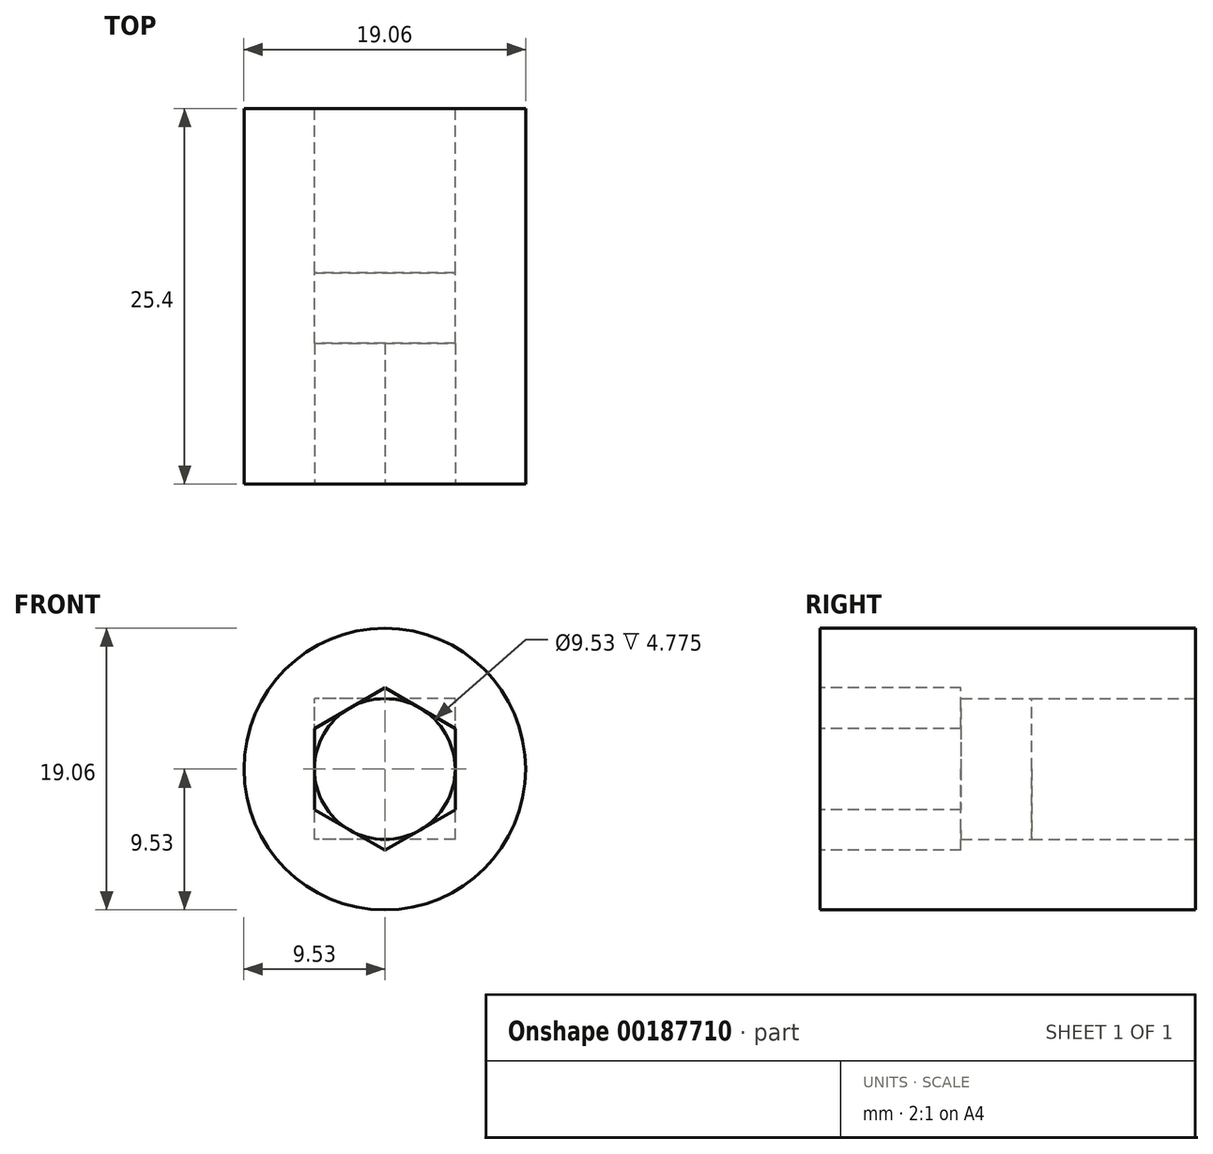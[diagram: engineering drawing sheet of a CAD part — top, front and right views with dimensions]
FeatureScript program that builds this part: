
annotation { "Feature Type Name" : "Feature", "Feature Type Description" : "" }
export const myFeature = defineFeature(function(context is Context, id is Id, definition is map)
    precondition{}
    {
        {
            var Q0;
            Q0=qCreatedBy(makeId("Front.planeOp"),FACE);
            var sketch = newSketch(context, id + "F0", { "sketchPlane" : qUnion([Q0])});
            skCircle(sketch, "E0", {"center": v(0, 0) * mm, "radius": 9.53 * mm});
            skSolve(sketch);
        }
        {
            var Q0;
            Q0=makeQuery(id+"F0.imprint","IMPRINT",FACE,{"disambiguationData":[TD([[makeQuery(id+"F0.imprint","IMPRINT",EDGE,{"derivedFrom":sQuery(id+"F0.wireOp",EDGE,"E0")}),1.0]])]});
            extrude(context, id + "F1", {"entities" : qUnion([Q0]), "depth" : 25.4 * mm});
        }
        {
            var Q0;
            Q0=qCreatedBy(makeId("Front.planeOp"),FACE);
            var sketch = newSketch(context, id + "F2", { "sketchPlane" : qUnion([Q0])});
            skLineSegment(sketch, "E1.bottom", {"start": v(4.76, -4.76) * mm, "end": v(-4.76, -4.76) * mm});
            skLineSegment(sketch, "E1.top", {"start": v(4.76, 4.76) * mm, "end": v(-4.76, 4.76) * mm});
            skLineSegment(sketch, "E1.left", {"start": v(4.76, -4.76) * mm, "end": v(4.76, 4.76) * mm});
            skLineSegment(sketch, "E1.right", {"start": v(-4.76, -4.76) * mm, "end": v(-4.76, 4.76) * mm});
            skPoint(sketch, "E1.middle", {"position": v(0, 0) * mm});
            skCircle(sketch, "E2", {"center": v(0, 0) * mm, "radius": 4.76 * mm});
            skSolve(sketch);
        }
        {
            var Q0;
            {var subQ0=sQuery(id+"F2.wireOp",EDGE,"E2");var subQ1=makeQuery(id+"F2.imprint","INTERSECT",VERTEX,{"derivedFrom":[sQuery(id+"F2.wireOp",EDGE,"E1.top"),subQ0]});Q0=makeQuery(id+"F2.imprint","IMPRINT",FACE,{"disambiguationData":[TD([[makeQuery(id+"F2.imprint","IMPRINT",EDGE,{"disambiguationData":[TD([[subQ1,1.0]])],"derivedFrom":subQ0}),1.0]])]});}
            var Q1;
            Q1=sQuery(id+"F2.wireOp",EDGE,"E2");
            extrude(context, id + "F3", {"entities" : qUnion([Q0]), "operationType" : NewBodyOperationType.REMOVE, "surfaceEntities" : qUnion([Q1]), "endBound" : BoundingType.THROUGH_ALL, "depth" : 25.4 * mm});
        }
        {
            var Q0;
            Q0 = qSketchRegion(id + "F2", true);
            extrude(context, id + "F4", {"entities" : qUnion([Q0]), "operationType" : NewBodyOperationType.REMOVE, "depth" : 11.1 * mm});
        }
        {
            var Q0;
            Q0=makeQuery(id+"F1.opExtrude","CAP_FACE",FACE,{"disambiguationData":[OSD([sQuery(id+"F0.wireOp",EDGE,"E0")])],"isStart":false});
            var sketch = newSketch(context, id + "F5", { "sketchPlane" : qUnion([Q0])});
            skCircle(sketch, "E3.cCircle", {"center": v(0, 0) * mm, "radius": 4.76 * mm, "construction": true});
            skLineSegment(sketch, "E3.0", {"start": v(4.76, 2.75) * mm, "end": v(4.76, -2.75) * mm});
            skLineSegment(sketch, "E3.1", {"start": v(4.76, -2.75) * mm, "end": v(0, -5.5) * mm});
            skLineSegment(sketch, "E3.2", {"start": v(0, -5.5) * mm, "end": v(-4.76, -2.75) * mm});
            skLineSegment(sketch, "E3.3", {"start": v(-4.76, -2.75) * mm, "end": v(-4.76, 2.75) * mm});
            skLineSegment(sketch, "E3.4", {"start": v(-4.76, 2.75) * mm, "end": v(0, 5.5) * mm});
            skLineSegment(sketch, "E3.5", {"start": v(0, 5.5) * mm, "end": v(4.76, 2.75) * mm});
            skPoint(sketch, "E3.0.midPoint", {"position": v(4.76, 0) * mm});
            skSolve(sketch);
        }
        {
            var Q0;
            {var subQ0=sQuery(id+"F5.wireOp",EDGE,"E3.5");var subQ1=sQuery(id+"F5.wireOp",EDGE,"E3.0");var subQ2=makeQuery(id+"F5.imprint","INTERSECT",VERTEX,{"derivedFrom":[subQ1,subQ0]});Q0=makeQuery(id+"F5.imprint","IMPRINT",FACE,{"disambiguationData":[TD([[makeQuery(id+"F5.imprint","IMPRINT",EDGE,{"disambiguationData":[TD([[subQ2,-1.0]])],"derivedFrom":subQ1}),-1.0]])]});}
            var Q1;
            {var subQ0=sQuery(id+"F5.wireOp",EDGE,"E3.5");var subQ1=sQuery(id+"F5.wireOp",EDGE,"E3.4");var subQ2=makeQuery(id+"F5.imprint","INTERSECT",VERTEX,{"derivedFrom":[subQ1,subQ0]});Q1=makeQuery(id+"F5.imprint","IMPRINT",FACE,{"disambiguationData":[TD([[makeQuery(id+"F5.imprint","IMPRINT",EDGE,{"disambiguationData":[TD([[subQ2,1.0]])],"derivedFrom":subQ1}),-1.0]])]});}
            var Q2;
            {var subQ0=sQuery(id+"F5.wireOp",EDGE,"E3.2");var subQ1=sQuery(id+"F5.wireOp",EDGE,"E3.1");var subQ2=makeQuery(id+"F5.imprint","INTERSECT",VERTEX,{"derivedFrom":[subQ1,subQ0]});Q2=makeQuery(id+"F5.imprint","IMPRINT",FACE,{"disambiguationData":[TD([[makeQuery(id+"F5.imprint","IMPRINT",EDGE,{"disambiguationData":[TD([[subQ2,1.0]])],"derivedFrom":subQ1}),-1.0]])]});}
            var Q3;
            {var subQ0=sQuery(id+"F5.wireOp",EDGE,"E3.1");var subQ1=sQuery(id+"F5.wireOp",EDGE,"E3.0");var subQ2=makeQuery(id+"F5.imprint","INTERSECT",VERTEX,{"derivedFrom":[subQ1,subQ0]});Q3=makeQuery(id+"F5.imprint","IMPRINT",FACE,{"disambiguationData":[TD([[makeQuery(id+"F5.imprint","IMPRINT",EDGE,{"disambiguationData":[TD([[subQ2,1.0]])],"derivedFrom":subQ1}),-1.0]])]});}
            var Q4;
            {var subQ0=sQuery(id+"F5.wireOp",EDGE,"E3.3");var subQ1=sQuery(id+"F5.wireOp",EDGE,"E3.2");var subQ2=makeQuery(id+"F5.imprint","INTERSECT",VERTEX,{"derivedFrom":[subQ1,subQ0]});Q4=makeQuery(id+"F5.imprint","IMPRINT",FACE,{"disambiguationData":[TD([[makeQuery(id+"F5.imprint","IMPRINT",EDGE,{"disambiguationData":[TD([[subQ2,1.0]])],"derivedFrom":subQ1}),-1.0]])]});}
            var Q5;
            {var subQ0=sQuery(id+"F5.wireOp",EDGE,"E3.4");var subQ1=sQuery(id+"F5.wireOp",EDGE,"E3.3");var subQ2=makeQuery(id+"F5.imprint","INTERSECT",VERTEX,{"derivedFrom":[subQ1,subQ0]});Q5=makeQuery(id+"F5.imprint","IMPRINT",FACE,{"disambiguationData":[TD([[makeQuery(id+"F5.imprint","IMPRINT",EDGE,{"disambiguationData":[TD([[subQ2,1.0]])],"derivedFrom":subQ1}),-1.0]])]});}
            var Q6;
            Q6=sQuery(id+"F5.wireOp",EDGE,"E3.3");
            var Q7;
            Q7=sQuery(id+"F5.wireOp",EDGE,"E3.4");
            var Q8;
            Q8=sQuery(id+"F5.wireOp",EDGE,"E3.5");
            var Q9;
            Q9=sQuery(id+"F5.wireOp",EDGE,"E3.0");
            var Q10;
            Q10=sQuery(id+"F5.wireOp",EDGE,"E3.1");
            var Q11;
            Q11=sQuery(id+"F5.wireOp",EDGE,"E3.2");
            extrude(context, id + "F6", {"entities" : qUnion([Q0, Q1, Q2, Q3, Q4, Q5]), "operationType" : NewBodyOperationType.REMOVE, "surfaceEntities" : qUnion([Q6, Q7, Q8, Q9, Q10, Q11]), "oppositeDirection" : true, "depth" : 9.52 * mm});
        }
    });
